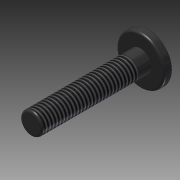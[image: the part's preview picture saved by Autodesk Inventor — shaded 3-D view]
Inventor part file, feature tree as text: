
AUTODESK INVENTOR PART (.ipt)
format: ipt  version: 2014 SP1 (Build 180222100, 222)  size: 122,880 bytes
history: native  units: in
note: dims shown in document units (in); Inventor stores cm internally (conversion verified against a paired STEP export)
features: sketch x2, revolve x1, fillet x1, extrude x1, thread x1
ambient origin geometry x8: Origin, YZ Plane, XZ Plane, XY Plane, X Axis, Y Axis, Z Axis, Center Point
bodies: Solid1 (feature_tree)
feature tree (6):
  revolve  "Revolution1"  [1 undecoded]
  fillet  "Fillet1"  Radius=0.2165in
  extrude  "Extrusion1"  TaperAngle=90.0deg  [1 undecoded]
  thread  "Thread1"  [1 undecoded]
  sketch  "Sketch1"  dims[d0=0.9843in d1=0.0787in d2=0.2165in]
  sketch  "Sketch2"  dims[d3=0.0984in d4=90.0deg d5=0.0197in d6=0.1181in d7=0.1181in d8=0.0in d9=1.1811in d10=0.1181in]
note: 3 required parameter values undecoded (feature->parameter linkage not recoverable at this tier; creation-order binding heuristic only, values carry confidence <= 0.55)